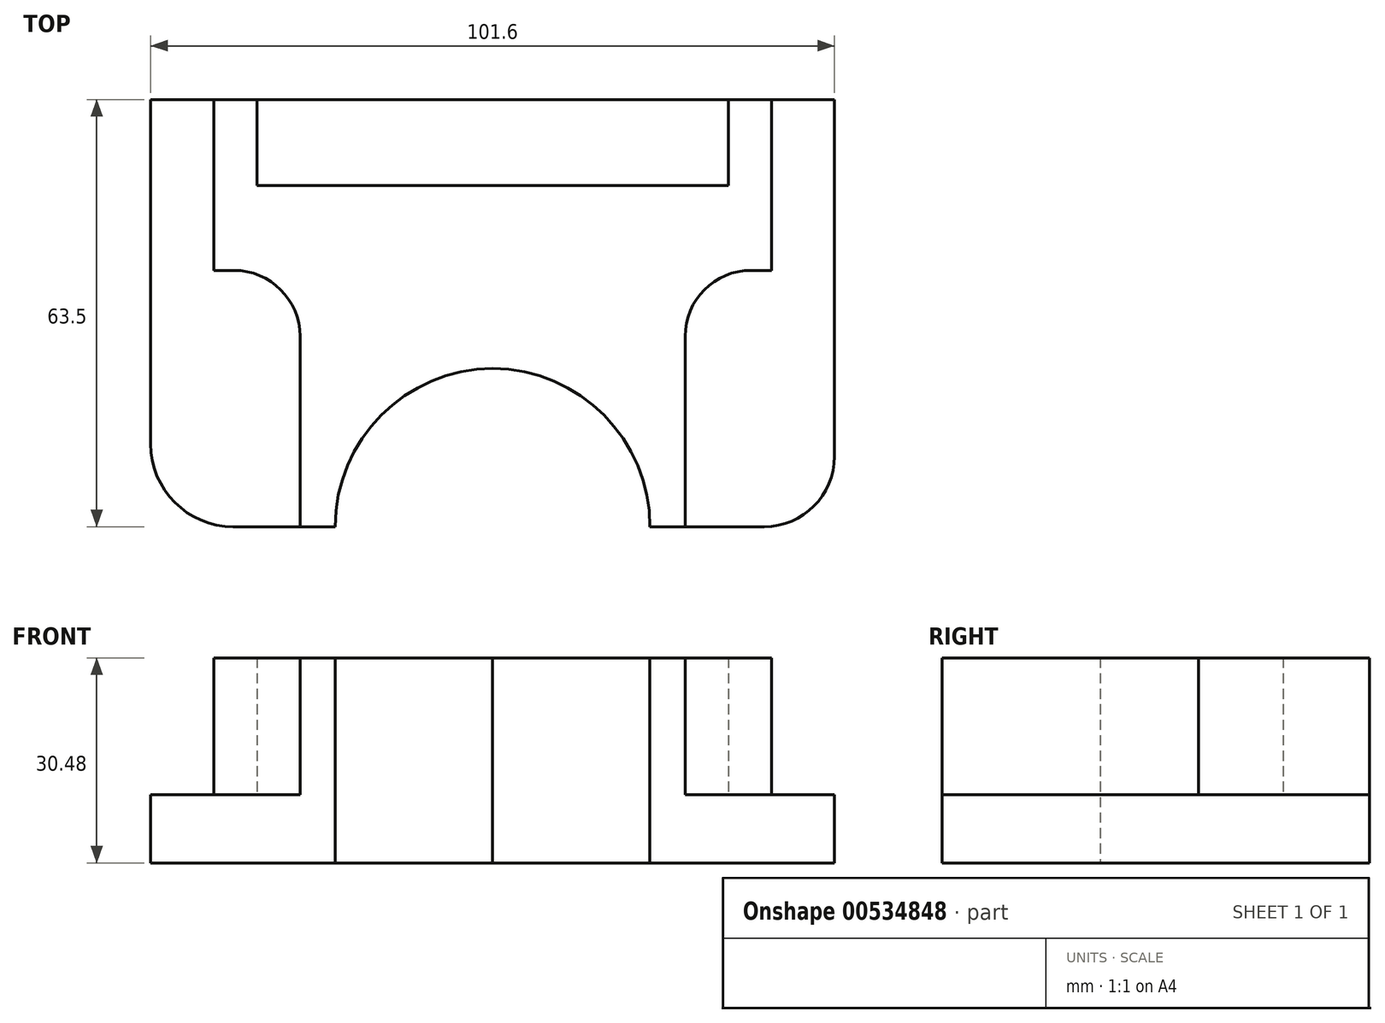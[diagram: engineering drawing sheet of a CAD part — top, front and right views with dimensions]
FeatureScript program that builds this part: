
annotation { "Feature Type Name" : "Feature", "Feature Type Description" : "" }
export const myFeature = defineFeature(function(context is Context, id is Id, definition is map)
    precondition{}
    {
        {
            var Q0;
            Q0=qCreatedBy(makeId("Top.planeOp"),FACE);
            var sketch = newSketch(context, id + "F0", { "sketchPlane" : qUnion([Q0])});
            skLineSegment(sketch, "E0.bottom", {"start": v(50.8, 31.75) * mm, "end": v(-50.8, 31.75) * mm});
            skLineSegment(sketch, "E0.top", {"start": v(50.8, -31.75) * mm, "end": v(-50.8, -31.75) * mm});
            skLineSegment(sketch, "E0.left", {"start": v(50.8, 31.75) * mm, "end": v(50.8, -31.75) * mm});
            skLineSegment(sketch, "E0.right", {"start": v(-50.8, 31.75) * mm, "end": v(-50.8, -31.75) * mm});
            skPoint(sketch, "E0.middle", {"position": v(0, 0) * mm});
            skSolve(sketch);
        }
        {
            var Q0;
            Q0 = qSketchRegion(id + "F0", true);
            extrude(context, id + "F1", {"entities" : qUnion([Q0]), "depth" : 10.16 * mm, "offsetDistance" : 25.4 * mm});
        }
        {
            var Q0;
            Q0=qCreatedBy(makeId("Top.planeOp"),FACE);
            var sketch = newSketch(context, id + "F2", { "sketchPlane" : qUnion([Q0])});
            skLineSegment(sketch, "E1", {"start": v(-41.43, 6.35) * mm, "end": v(-41.43, 31.75) * mm});
            skLineSegment(sketch, "E2", {"start": v(-41.43, 31.75) * mm, "end": v(-35.02, 31.75) * mm});
            skLineSegment(sketch, "E3", {"start": v(-35.02, 31.75) * mm, "end": v(-35.02, 18.93) * mm});
            skLineSegment(sketch, "E4", {"start": v(-41.43, 6.35) * mm, "end": v(-28.61, 6.35) * mm});
            skLineSegment(sketch, "E5", {"start": v(-28.61, 6.35) * mm, "end": v(-28.61, -31.75) * mm});
            skLineSegment(sketch, "E6", {"start": v(-28.61, -31.75) * mm, "end": v(-23.38, -31.75) * mm});
            skLineSegment(sketch, "E7", {"start": v(-35.02, 18.93) * mm, "end": v(0, 18.93) * mm});
            skLineSegment(sketch, "E8.MirrorCS", {"start": v(28.61, -31.75) * mm, "end": v(23.38, -31.75) * mm});
            skLineSegment(sketch, "E9.MirrorCS", {"start": v(28.61, 6.35) * mm, "end": v(28.61, -31.75) * mm});
            skLineSegment(sketch, "E10.MirrorCS", {"start": v(41.43, 6.35) * mm, "end": v(28.61, 6.35) * mm});
            skLineSegment(sketch, "E11.MirrorCS", {"start": v(41.43, 6.35) * mm, "end": v(41.43, 31.75) * mm});
            skLineSegment(sketch, "E12.MirrorCS", {"start": v(41.43, 31.75) * mm, "end": v(35.02, 31.75) * mm});
            skLineSegment(sketch, "E13.MirrorCS", {"start": v(35.02, 18.93) * mm, "end": v(0, 18.93) * mm});
            skLineSegment(sketch, "E14.MirrorCS", {"start": v(35.02, 31.75) * mm, "end": v(35.02, 18.93) * mm});
            skArc(sketch, "E15", {"start": v(0, -8.24) * mm, "mid": v(-16.54, -15.17) * mm, "end": v(-23.38, -31.75) * mm});
            skArc(sketch, "E16.MirrorCS", {"start": v(0, -8.24) * mm, "mid": v(16.54, -15.17) * mm, "end": v(23.38, -31.75) * mm});
            skSolve(sketch);
        }
        {
            var Q0;
            Q0 = qSketchRegion(id + "F2", true);
            extrude(context, id + "F3", {"entities" : qUnion([Q0]), "operationType" : NewBodyOperationType.ADD, "depth" : 30.48 * mm, "offsetDistance" : 25.4 * mm});
        }
        {
            var Q0;
            {var subQ0=sQuery(id+"F0.wireOp",EDGE,"E0.top");Q0=makeQuery(id+"F3.boolean.opBoolean","SPLIT",FACE,{"disambiguationData":[TD([makeQuery(id+"F3.opExtrude","SWEPT_FACE",FACE,{"disambiguationData":[OSD([sQuery(id+"F2.wireOp",EDGE,"E15")])]})])],"derivedFrom":makeQuery(id+"F1.opExtrude","CAP_FACE",FACE,{"disambiguationData":[OSD([sQuery(id+"F0.wireOp",EDGE,"E0.bottom"),subQ0,sQuery(id+"F0.wireOp",EDGE,"E0.left"),sQuery(id+"F0.wireOp",EDGE,"E0.right")])],"isStart":false})});}
            extrude(context, id + "F4", {"entities" : qUnion([Q0]), "operationType" : NewBodyOperationType.REMOVE, "oppositeDirection" : true, "depth" : 25.4 * mm, "offsetDistance" : 25.4 * mm});
        }
        {
            var Q0;
            Q0=makeQuery(id+"F1.opExtrude","SWEPT_EDGE",EDGE,{"disambiguationData":[OSD([sQuery(id+"F0.wireOp",EDGE,"E0.top"),sQuery(id+"F0.wireOp",EDGE,"E0.left")])]});
            fillet(context, id + "F5", {"entities" : qUnion([Q0]), "radius" : 10.42 * mm, "tangentPropagation" : true, "allowEdgeOverflow" : false});
        }
        {
            var Q0;
            Q0=makeQuery(id+"F1.opExtrude","SWEPT_EDGE",EDGE,{"disambiguationData":[OSD([sQuery(id+"F0.wireOp",EDGE,"E0.top"),sQuery(id+"F0.wireOp",EDGE,"E0.right")])]});
            fillet(context, id + "F6", {"entities" : qUnion([Q0]), "radius" : 12.26 * mm, "tangentPropagation" : true, "allowEdgeOverflow" : false});
        }
        {
            var Q0;
            Q0=makeQuery(id+"F3.opExtrude","SWEPT_EDGE",EDGE,{"disambiguationData":[OSD([sQuery(id+"F2.wireOp",EDGE,"E9.MirrorCS"),sQuery(id+"F2.wireOp",EDGE,"E10.MirrorCS")])]});
            var Q1;
            Q1=makeQuery(id+"F3.opExtrude","SWEPT_EDGE",EDGE,{"disambiguationData":[OSD([sQuery(id+"F2.wireOp",EDGE,"E4"),sQuery(id+"F2.wireOp",EDGE,"E5")])]});
            fillet(context, id + "F7", {"entities" : qUnion([Q0, Q1]), "radius" : 9.8 * mm, "tangentPropagation" : true, "allowEdgeOverflow" : false});
        }
    });
